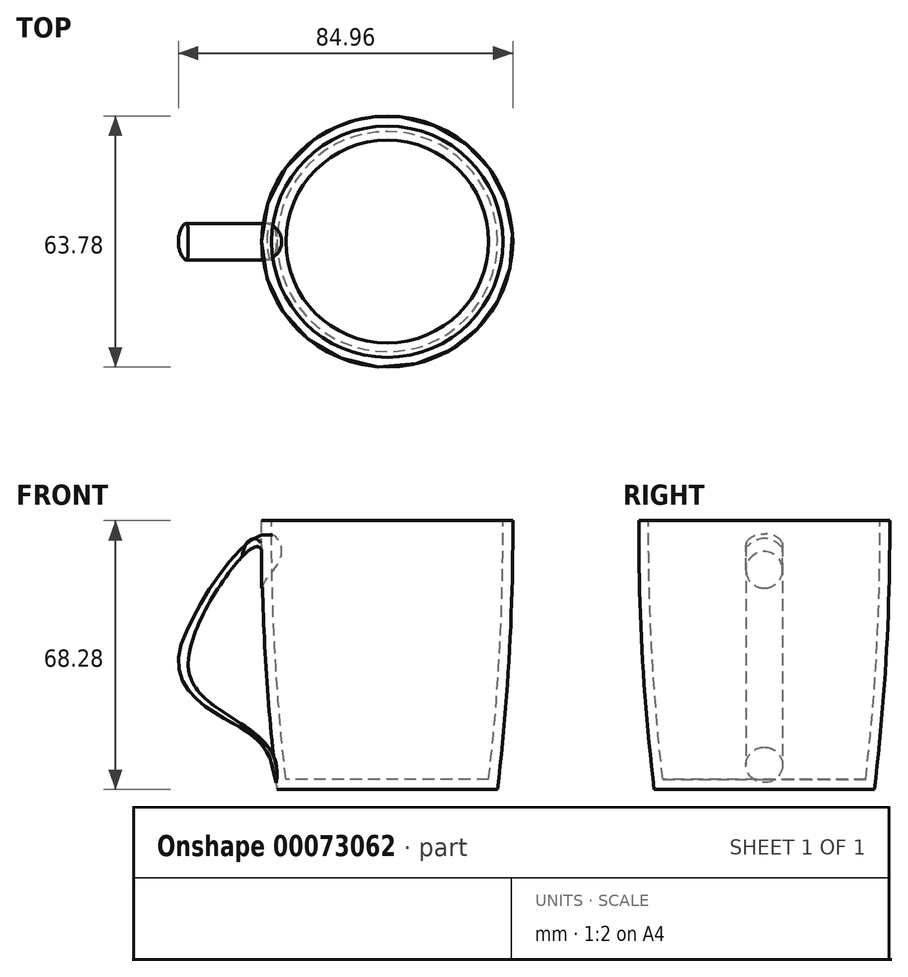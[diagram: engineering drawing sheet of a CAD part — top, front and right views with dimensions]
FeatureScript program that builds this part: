
annotation { "Feature Type Name" : "Feature", "Feature Type Description" : "" }
export const myFeature = defineFeature(function(context is Context, id is Id, definition is map)
    precondition{}
    {
        {
            var Q0;
            Q0=qCreatedBy(makeId("Front.planeOp"),FACE);
            var sketch = newSketch(context, id + "F0", { "sketchPlane" : qUnion([Q0])});
            skArc(sketch, "E0", {"start": v(0, 34.74) * mm, "mid": v(0.89, 0.54) * mm, "end": v(3.9, -33.54) * mm});
            skLineSegment(sketch, "E1", {"start": v(0, 34.74) * mm, "end": v(31.88, 34.74) * mm});
            skLineSegment(sketch, "E2", {"start": v(31.88, 34.74) * mm, "end": v(31.88, -26.32) * mm});
            skLineSegment(sketch, "E3", {"start": v(3.9, -33.54) * mm, "end": v(31.88, -33.54) * mm});
            skLineSegment(sketch, "E4", {"start": v(31.88, -33.54) * mm, "end": v(31.88, -26.32) * mm});
            skSolve(sketch);
        }
        {
            var Q0;
            Q0 = qSketchRegion(id + "F0", true);
            var Q1;
            Q1=sQuery(id+"F0.wireOp",EDGE,"E2");
            revolve(context, id + "F1", {"entities" : qUnion([Q0]), "axis" : qUnion([Q1]), "revolveType" : RevolveType.FULL, "oppositeDirection" : true});
        }
        {
            var Q0;
            Q0=makeQuery(id+"F1.opRevolve","SWEPT_FACE",FACE,{"disambiguationData":[OSD([sQuery(id+"F0.wireOp",EDGE,"E1")])]});
            shell(context, id + "F2", {"entities" : qUnion([Q0]), "thickness" : 2.5 * mm});
        }
        {
            var Q0;
            Q0=qCreatedBy(makeId("Front.planeOp"),FACE);
            var sketch = newSketch(context, id + "F3", { "sketchPlane" : qUnion([Q0])});
            skFitSpline(sketch, "E5", {"points": [v(0, 23.48) * mm, v(-18.9, 0) * mm, v(2.82, -28.54) * mm], "startDerivative": vector(15.86, 94.36) * mm, "endDerivative": vector(5.18, -72.73) * mm});
            skSolve(sketch);
        }
        {
            var Q0;
            Q0=qCreatedBy(makeId("Right.planeOp"),FACE);
            var sketch = newSketch(context, id + "F4", { "sketchPlane" : qUnion([Q0])});
            skCircle(sketch, "E6", {"center": v(0, 22.23) * mm, "radius": 4.64 * mm});
            skSolve(sketch);
        }
        {
            var Q0;
            Q0=makeQuery(id+"F4.imprint","IMPRINT",FACE,{"disambiguationData":[TD([[makeQuery(id+"F4.imprint","IMPRINT",EDGE,{"derivedFrom":sQuery(id+"F4.wireOp",EDGE,"E6")}),1.0]])]});
            var Q1;
            Q1=sQuery(id+"F3.wireOp",EDGE,"E5");
            sweep(context, id + "F5", {"profiles" : qUnion([Q0]), "path" : qUnion([Q1])});
        }
    });
